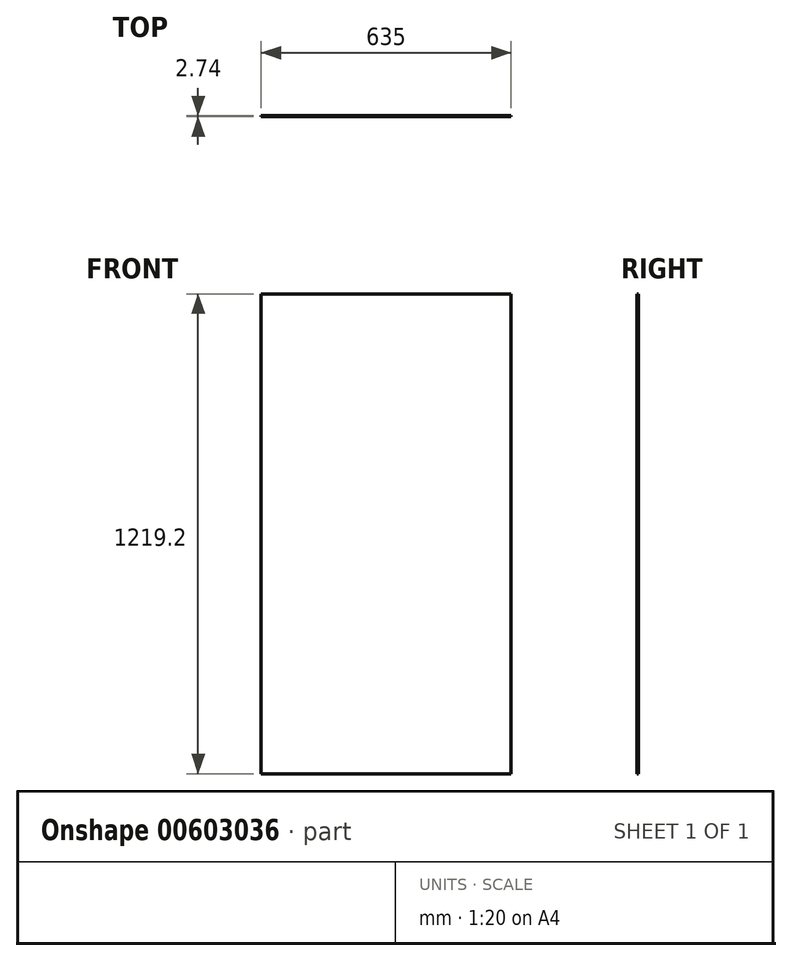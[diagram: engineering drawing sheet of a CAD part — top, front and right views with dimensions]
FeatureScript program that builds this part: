
annotation { "Feature Type Name" : "Feature", "Feature Type Description" : "" }
export const myFeature = defineFeature(function(context is Context, id is Id, definition is map)
    precondition{}
    {
        {
            var Q0;
            Q0=qCreatedBy(makeId("Front.planeOp"), FACE);
            var sketch = newSketch(context, id + "F0", { "sketchPlane" : qUnion([Q0])});
            skLineSegment(sketch, "E0.bottom", {"start": v(317.5, -609.6) * mm, "end": v(-317.5, -609.6) * mm});
            skLineSegment(sketch, "E0.top", {"start": v(317.5, 609.6) * mm, "end": v(-317.5, 609.6) * mm});
            skLineSegment(sketch, "E0.left", {"start": v(317.5, -609.6) * mm, "end": v(317.5, 609.6) * mm});
            skLineSegment(sketch, "E0.right", {"start": v(-317.5, -609.6) * mm, "end": v(-317.5, 609.6) * mm});
            skPoint(sketch, "E0.middle", {"position": v(0, 0) * mm});
            skSolve(sketch);
        }
        {
            var Q0;
            Q0 = qSketchRegion(id + "F0", true);
            extrude(context, id + "F1", {"entities" : qUnion([Q0]), "depth" : 2.74 * mm, "offsetDistance" : 25.4 * mm});
        }
    });
